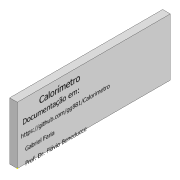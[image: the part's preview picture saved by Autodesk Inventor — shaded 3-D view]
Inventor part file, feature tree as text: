
AUTODESK INVENTOR PART (.ipt)
format: ipt  version: 2020 (Build 240168000, 168)  size: 82,944 bytes
history: native  units: mm
features: sketch x2, other x1, extrude x1
ambient origin geometry x8: Origin, YZ Plane, XZ Plane, XY Plane, X Axis, Y Axis, Z Axis, Center Point
bodies: Body1 (feature_tree)
feature tree (4):
  other  "Sólido1"
  extrude  "Extrusão1"  Depth=30.0mm
  sketch  "Esboço2"  dims[d2=4.0mm d3=0.0mm]
  sketch  "Esboço1"  dims[d0=80.0mm d1=30.0mm]
